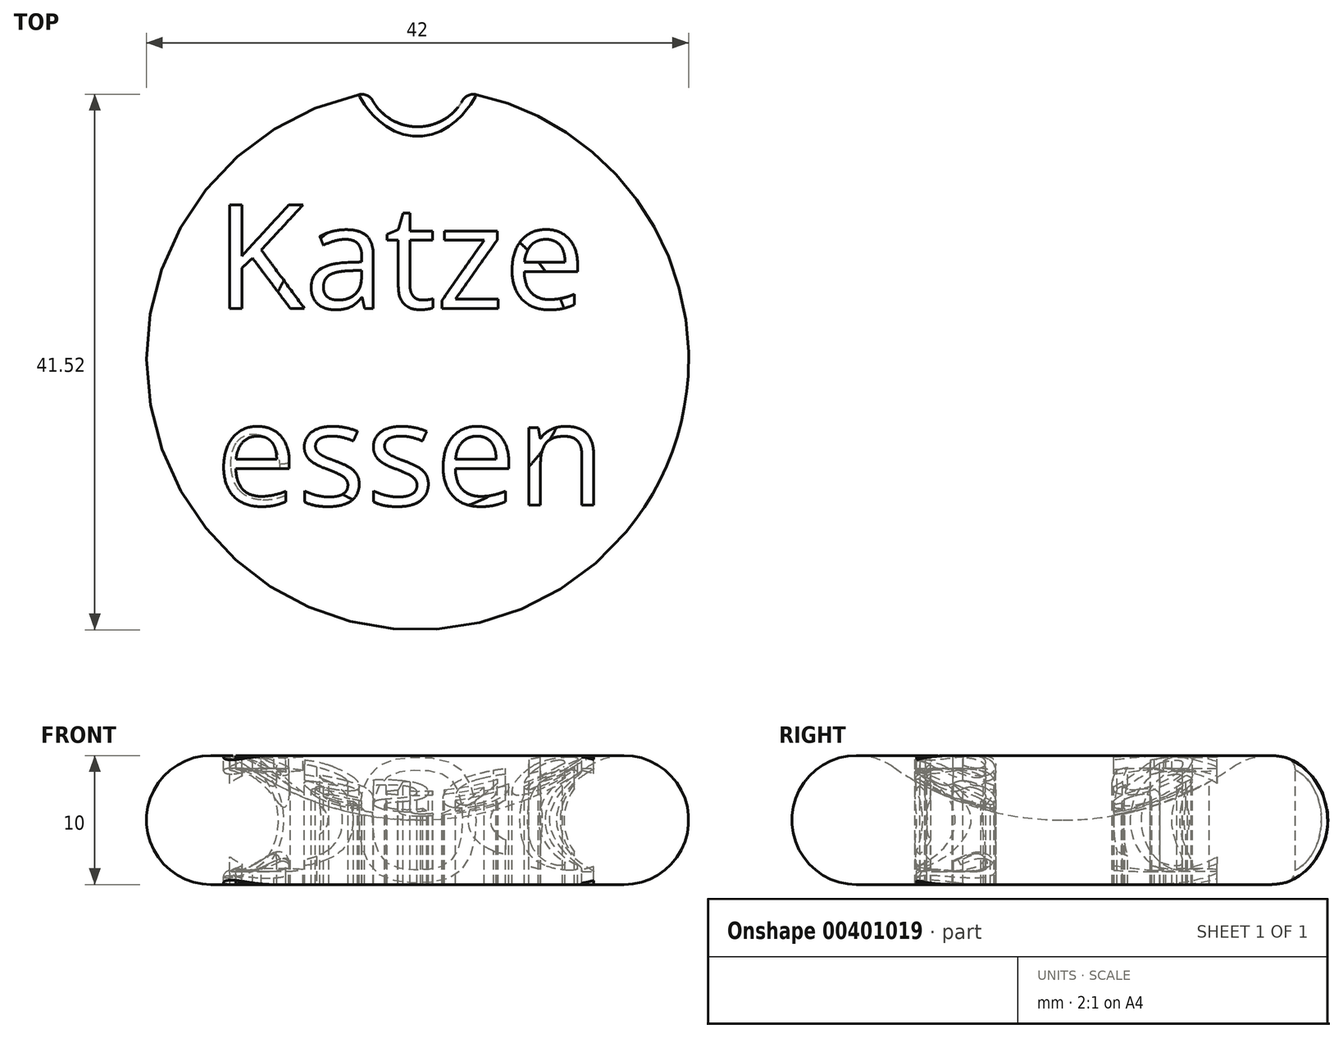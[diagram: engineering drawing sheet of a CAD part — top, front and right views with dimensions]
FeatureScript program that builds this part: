
annotation { "Feature Type Name" : "Feature", "Feature Type Description" : "" }
export const myFeature = defineFeature(function(context is Context, id is Id, definition is map)
    precondition{}
    {
        {
            var Q0;
            Q0=qCreatedBy(makeId("Front.planeOp"),FACE);
            var sketch = newSketch(context, id + "F0", { "sketchPlane" : qUnion([Q0])});
            skArc(sketch, "E0", {"start": v(-13.15, 9.11) * mm, "mid": v(-6.9, 6.05) * mm, "end": v(0, 5) * mm});
            skArc(sketch, "E1", {"start": v(-13.15, 9.11) * mm, "mid": v(-20.77, 6.5) * mm, "end": v(-16, 0) * mm});
            skLineSegment(sketch, "E2", {"start": v(0, 0) * mm, "end": v(-16, 0) * mm});
            skLineSegment(sketch, "E3", {"start": v(0, 5) * mm, "end": v(0, 0) * mm});
            skSolve(sketch);
        }
        {
            var Q0;
            Q0=makeQuery(id+"F0.imprint","IMPRINT",FACE,{"disambiguationData":[TD([[makeQuery(id+"F0.imprint","IMPRINT",EDGE,{"derivedFrom":sQuery(id+"F0.wireOp",EDGE,"E0")}),-1.0]])]});
            var Q1;
            Q1=sQuery(id+"F0.wireOp",EDGE,"E3");
            revolve(context, id + "F1", {"entities" : qUnion([Q0]), "axis" : qUnion([Q1]), "revolveType" : RevolveType.FULL});
        }
        {
            var Q0;
            Q0=qCreatedBy(makeId("Top.planeOp"),FACE);
            cPlane(context, id + "F2", {"entities" : qUnion([Q0]), "cplaneType" : CPlaneType.OFFSET, "offset" : 15 * mm, "width" : 150 * mm, "height" : 150 * mm});
        }
        {
            var Q0;
            Q0=qCreatedBy(id+"F2.planeOp",FACE);
            var sketch = newSketch(context, id + "F3", { "sketchPlane" : qUnion([Q0])});
            skText(sketch, "E4", { "text": "Katze\nessen", "fontName": "OpenSans-Regular.ttf"});
            const initialGuessF3  = {"E4": [-0.01565, 0.00392, 1, 0, 0.00808]};
            skSetInitialGuess(sketch, initialGuessF3);
            skSolve(sketch);
        }
        {
            var Q0;
            Q0 = qSketchRegion(id + "F3", true);
            extrude(context, id + "F4", {"entities" : qUnion([Q0]), "operationType" : NewBodyOperationType.REMOVE, "oppositeDirection" : true, "depth" : 25 * mm});
        }
        {
            var Q0;
            Q0=qCreatedBy(makeId("Front.planeOp"),FACE);
            var sketch = newSketch(context, id + "F5", { "sketchPlane" : qUnion([Q0])});
            skCircle(sketch, "E5", {"center": v(-16, 5) * mm, "radius": 4 * mm});
            skSolve(sketch);
        }
        {
            var Q0;
            Q0 = qSketchRegion(id + "F5", true);
            var Q1;
            Q1=sQuery(id+"F5.wireOp",EDGE,"E5");
            var Q2;
            Q2=sQuery(id+"F0.wireOp",EDGE,"E3");
            revolve(context, id + "F6", {"operationType" : NewBodyOperationType.ADD, "entities" : qUnion([Q0]), "surfaceEntities" : qUnion([Q1]), "axis" : qUnion([Q2]), "revolveType" : RevolveType.FULL});
        }
        {
            var Q0;
            Q0=qCreatedBy(id+"F2.planeOp",FACE);
            var sketch = newSketch(context, id + "F7", { "sketchPlane" : qUnion([Q0])});
            skCircle(sketch, "E6", {"center": v(0, 22) * mm, "radius": 4 * mm});
            skSolve(sketch);
        }
        {
            var Q0;
            Q0 = qSketchRegion(id + "F7", true);
            extrude(context, id + "F8", {"entities" : qUnion([Q0]), "operationType" : NewBodyOperationType.REMOVE, "oppositeDirection" : true, "depth" : 25 * mm});
        }
        {
            var Q0;
            Q0=makeQuery(id+"F8.boolean.opBoolean","INTERSECT",EDGE,{"derivedFrom":[makeQuery(id+"F4.boolean.opBoolean","SPLIT",FACE,{"disambiguationData":[TD([makeQuery(id+"F1.opRevolve","SWEPT_FACE",FACE,{"disambiguationData":[OSD([sQuery(id+"F0.wireOp",EDGE,"E0")])]}),makeQuery(id+"F1.opRevolve","SWEPT_FACE",FACE,{"disambiguationData":[OSD([sQuery(id+"F0.wireOp",EDGE,"E2")])]}),makeQuery(id+"F4.opExtrude","SWEPT_FACE",FACE,{"disambiguationData":[OSD([sQuery(id+"F3.wireOp",EDGE,"E4.sketch_text.stroke-1")])]}),makeQuery(id+"F4.opExtrude","SWEPT_FACE",FACE,{"disambiguationData":[OSD([sQuery(id+"F3.wireOp",EDGE,"E4.sketch_text.stroke-2")])]}),makeQuery(id+"F4.opExtrude","SWEPT_FACE",FACE,{"disambiguationData":[OSD([sQuery(id+"F3.wireOp",EDGE,"E4.sketch_text.stroke-3")])]}),makeQuery(id+"F4.opExtrude","SWEPT_FACE",FACE,{"disambiguationData":[OSD([sQuery(id+"F3.wireOp",EDGE,"E4.sketch_text.stroke-4")])]}),makeQuery(id+"F4.opExtrude","SWEPT_FACE",FACE,{"disambiguationData":[OSD([sQuery(id+"F3.wireOp",EDGE,"E4.sketch_text.stroke-5")])]}),makeQuery(id+"F4.opExtrude","SWEPT_FACE",FACE,{"disambiguationData":[OSD([sQuery(id+"F3.wireOp",EDGE,"E4.sketch_text.stroke-6")])]}),makeQuery(id+"F4.opExtrude","SWEPT_FACE",FACE,{"disambiguationData":[OSD([sQuery(id+"F3.wireOp",EDGE,"E4.sketch_text.stroke-7")])]}),makeQuery(id+"F4.opExtrude","SWEPT_FACE",FACE,{"disambiguationData":[OSD([sQuery(id+"F3.wireOp",EDGE,"E4.sketch_text.stroke-8")])]}),makeQuery(id+"F4.opExtrude","SWEPT_FACE",FACE,{"disambiguationData":[OSD([sQuery(id+"F3.wireOp",EDGE,"E4.sketch_text.stroke-9")])]}),makeQuery(id+"F4.opExtrude","SWEPT_FACE",FACE,{"disambiguationData":[OSD([sQuery(id+"F3.wireOp",EDGE,"E4.sketch_text.stroke-10")])]}),makeQuery(id+"F4.opExtrude","SWEPT_FACE",FACE,{"disambiguationData":[OSD([sQuery(id+"F3.wireOp",EDGE,"E4.sketch_text.stroke-11")])]}),makeQuery(id+"F4.opExtrude","SWEPT_FACE",FACE,{"disambiguationData":[OSD([sQuery(id+"F3.wireOp",EDGE,"E4.sketch_text.stroke-71")])]}),makeQuery(id+"F4.opExtrude","SWEPT_FACE",FACE,{"disambiguationData":[OSD([sQuery(id+"F3.wireOp",EDGE,"E4.sketch_text.stroke-72")])]}),makeQuery(id+"F4.opExtrude","SWEPT_FACE",FACE,{"disambiguationData":[OSD([sQuery(id+"F3.wireOp",EDGE,"E4.sketch_text.stroke-73")])]}),makeQuery(id+"F4.opExtrude","SWEPT_FACE",FACE,{"disambiguationData":[OSD([sQuery(id+"F3.wireOp",EDGE,"E4.sketch_text.stroke-74")])]}),makeQuery(id+"F4.opExtrude","SWEPT_FACE",FACE,{"disambiguationData":[OSD([sQuery(id+"F3.wireOp",EDGE,"E4.sketch_text.stroke-75")])]}),makeQuery(id+"F4.opExtrude","SWEPT_FACE",FACE,{"disambiguationData":[OSD([sQuery(id+"F3.wireOp",EDGE,"E4.sketch_text.stroke-87")])]}),makeQuery(id+"F4.opExtrude","SWEPT_FACE",FACE,{"disambiguationData":[OSD([sQuery(id+"F3.wireOp",EDGE,"E4.sketch_text.stroke-88")])]}),makeQuery(id+"F4.opExtrude","SWEPT_FACE",FACE,{"disambiguationData":[OSD([sQuery(id+"F3.wireOp",EDGE,"E4.sketch_text.stroke-89")])]}),makeQuery(id+"F4.opExtrude","SWEPT_FACE",FACE,{"disambiguationData":[OSD([sQuery(id+"F3.wireOp",EDGE,"E4.sketch_text.stroke-90")])]}),makeQuery(id+"F4.opExtrude","SWEPT_FACE",FACE,{"disambiguationData":[OSD([sQuery(id+"F3.wireOp",EDGE,"E4.sketch_text.stroke-91")])]}),makeQuery(id+"F4.opExtrude","SWEPT_FACE",FACE,{"disambiguationData":[OSD([sQuery(id+"F3.wireOp",EDGE,"E4.sketch_text.stroke-94")])]}),makeQuery(id+"F4.opExtrude","SWEPT_FACE",FACE,{"disambiguationData":[OSD([sQuery(id+"F3.wireOp",EDGE,"E4.sketch_text.stroke-95")])]}),makeQuery(id+"F4.opExtrude","SWEPT_FACE",FACE,{"disambiguationData":[OSD([sQuery(id+"F3.wireOp",EDGE,"E4.sketch_text.stroke-96")])]}),makeQuery(id+"F4.opExtrude","SWEPT_FACE",FACE,{"disambiguationData":[OSD([sQuery(id+"F3.wireOp",EDGE,"E4.sketch_text.stroke-97")])]}),makeQuery(id+"F4.opExtrude","SWEPT_FACE",FACE,{"disambiguationData":[OSD([sQuery(id+"F3.wireOp",EDGE,"E4.sketch_text.stroke-98")])]}),makeQuery(id+"F4.opExtrude","SWEPT_FACE",FACE,{"disambiguationData":[OSD([sQuery(id+"F3.wireOp",EDGE,"E4.sketch_text.stroke-99")])]}),makeQuery(id+"F4.opExtrude","SWEPT_FACE",FACE,{"disambiguationData":[OSD([sQuery(id+"F3.wireOp",EDGE,"E4.sketch_text.stroke-100")])]}),makeQuery(id+"F4.opExtrude","SWEPT_FACE",FACE,{"disambiguationData":[OSD([sQuery(id+"F3.wireOp",EDGE,"E4.sketch_text.stroke-107")])]}),makeQuery(id+"F4.opExtrude","SWEPT_FACE",FACE,{"disambiguationData":[OSD([sQuery(id+"F3.wireOp",EDGE,"E4.sketch_text.stroke-108")])]}),makeQuery(id+"F4.opExtrude","SWEPT_FACE",FACE,{"disambiguationData":[OSD([sQuery(id+"F3.wireOp",EDGE,"E4.sketch_text.stroke-109")])]}),makeQuery(id+"F4.opExtrude","SWEPT_FACE",FACE,{"disambiguationData":[OSD([sQuery(id+"F3.wireOp",EDGE,"E4.sketch_text.stroke-110")])]}),makeQuery(id+"F4.opExtrude","SWEPT_FACE",FACE,{"disambiguationData":[OSD([sQuery(id+"F3.wireOp",EDGE,"E4.sketch_text.stroke-111")])]}),makeQuery(id+"F4.opExtrude","SWEPT_FACE",FACE,{"disambiguationData":[OSD([sQuery(id+"F3.wireOp",EDGE,"E4.sketch_text.stroke-175")])]}),makeQuery(id+"F4.opExtrude","SWEPT_FACE",FACE,{"disambiguationData":[OSD([sQuery(id+"F3.wireOp",EDGE,"E4.sketch_text.stroke-176")])]}),makeQuery(id+"F4.opExtrude","SWEPT_FACE",FACE,{"disambiguationData":[OSD([sQuery(id+"F3.wireOp",EDGE,"E4.sketch_text.stroke-177")])]}),makeQuery(id+"F4.opExtrude","SWEPT_FACE",FACE,{"disambiguationData":[OSD([sQuery(id+"F3.wireOp",EDGE,"E4.sketch_text.stroke-180")])]}),makeQuery(id+"F4.opExtrude","SWEPT_FACE",FACE,{"disambiguationData":[OSD([sQuery(id+"F3.wireOp",EDGE,"E4.sketch_text.stroke-181")])]}),makeQuery(id+"F4.opExtrude","SWEPT_FACE",FACE,{"disambiguationData":[OSD([sQuery(id+"F3.wireOp",EDGE,"E4.sketch_text.stroke-182")])]}),makeQuery(id+"F4.opExtrude","SWEPT_FACE",FACE,{"disambiguationData":[OSD([sQuery(id+"F3.wireOp",EDGE,"E4.sketch_text.stroke-188")])]}),makeQuery(id+"F4.opExtrude","SWEPT_FACE",FACE,{"disambiguationData":[OSD([sQuery(id+"F3.wireOp",EDGE,"E4.sketch_text.stroke-189")])]}),makeQuery(id+"F4.opExtrude","SWEPT_FACE",FACE,{"disambiguationData":[OSD([sQuery(id+"F3.wireOp",EDGE,"E4.sketch_text.stroke-190")])]}),makeQuery(id+"F4.opExtrude","SWEPT_FACE",FACE,{"disambiguationData":[OSD([sQuery(id+"F3.wireOp",EDGE,"E4.sketch_text.stroke-191")])]})])],"derivedFrom":makeQuery(id+"F1.opRevolve","SWEPT_FACE",FACE,{"disambiguationData":[OSD([sQuery(id+"F0.wireOp",EDGE,"E1")])]})}),makeQuery(id+"F8.opExtrude","SWEPT_FACE",FACE,{"disambiguationData":[OSD([sQuery(id+"F7.wireOp",EDGE,"E6")])]})]});
            fillet(context, id + "F9", {"entities" : qUnion([Q0]), "radius" : 1 * mm, "tangentPropagation" : true, "allowEdgeOverflow" : false});
        }
        {
            var Q0;
            Q0=makeQuery(id+"F6.boolean.opBoolean","INTERSECT",EDGE,{"disambiguationData":[OD(0.0)],"derivedFrom":[makeQuery(id+"F4.boolean.opBoolean","COPY",FACE,{"derivedFrom":makeQuery(id+"F4.opExtrude","SWEPT_FACE",FACE,{"disambiguationData":[OSD([sQuery(id+"F3.wireOp",EDGE,"E4.sketch_text.stroke-88")])]})}),makeQuery(id+"F6.opRevolve","SWEPT_FACE",FACE,{"disambiguationData":[OSD([sQuery(id+"F5.wireOp",EDGE,"E5")])]})]});
            fillet(context, id + "F10", {"entities" : qUnion([Q0]), "radius" : 0.5 * mm, "tangentPropagation" : true, "allowEdgeOverflow" : false});
        }
    });
